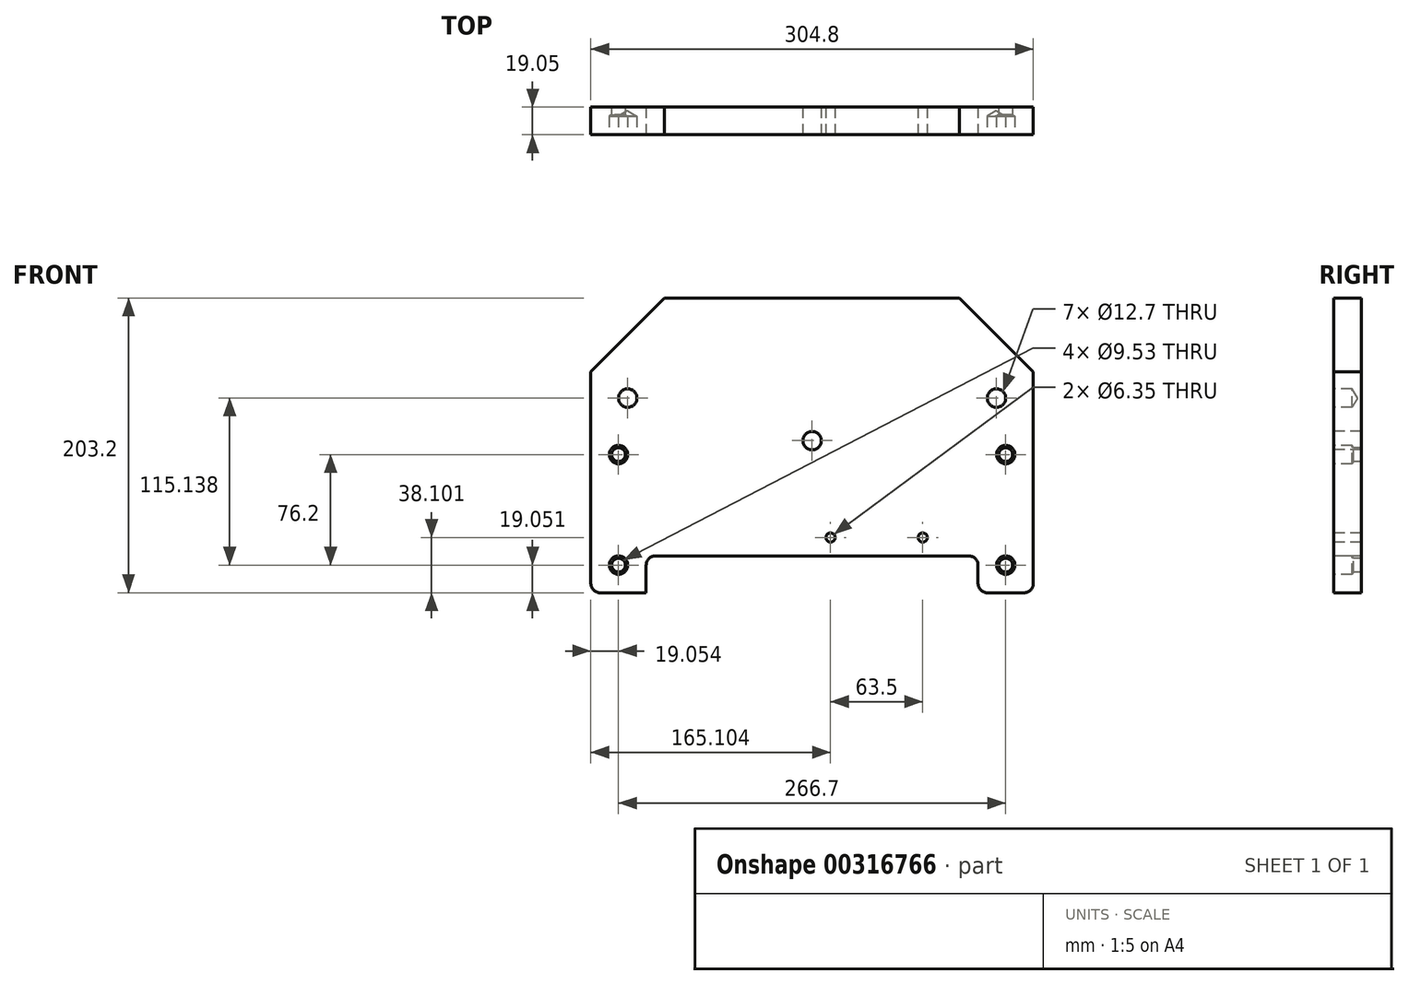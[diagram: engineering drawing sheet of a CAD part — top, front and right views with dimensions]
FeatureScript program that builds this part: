
annotation { "Feature Type Name" : "Feature", "Feature Type Description" : "" }
export const myFeature = defineFeature(function(context is Context, id is Id, definition is map)
    precondition{}
    {
        {
            var Q0;
            Q0=qCreatedBy(makeId("Front.planeOp"),FACE);
            var sketch = newSketch(context, id + "F0", { "sketchPlane" : qUnion([Q0])});
            skLineSegment(sketch, "E0.bottom", {"start": v(-130.02, 132.17) * mm, "end": v(174.78, 132.17) * mm});
            skLineSegment(sketch, "E0.top", {"start": v(-130.02, -71.03) * mm, "end": v(174.78, -71.03) * mm});
            skLineSegment(sketch, "E0.left", {"start": v(-130.02, 132.17) * mm, "end": v(-130.02, -71.03) * mm});
            skLineSegment(sketch, "E0.right", {"start": v(174.78, 132.17) * mm, "end": v(174.78, -71.03) * mm});
            skSolve(sketch);
        }
        {
            var Q0;
            Q0=makeQuery(id+"F0.imprint","IMPRINT",FACE,{"disambiguationData":[TD([[makeQuery(id+"F0.imprint","IMPRINT",EDGE,{"derivedFrom":sQuery(id+"F0.wireOp",EDGE,"E0.bottom")}),-1.0]])]});
            extrude(context, id + "F1", {"entities" : qUnion([Q0]), "depth" : 19.05 * mm});
        }
        {
            var Q0;
            Q0=makeQuery(id+"F1.opExtrude","SWEPT_EDGE",EDGE,{"disambiguationData":[OSD([sQuery(id+"F0.wireOp",EDGE,"E0.bottom"),sQuery(id+"F0.wireOp",EDGE,"E0.left")])]});
            var Q1;
            Q1=makeQuery(id+"F1.opExtrude","SWEPT_EDGE",EDGE,{"disambiguationData":[OSD([sQuery(id+"F0.wireOp",EDGE,"E0.bottom"),sQuery(id+"F0.wireOp",EDGE,"E0.right")])]});
            chamfer(context, id + "F2", {"entities" : qUnion([Q0, Q1]), "width" : 50.8 * mm, "tangentPropagation" : true});
        }
        {
            var Q0;
            Q0=makeQuery(id+"F1.opExtrude","CAP_FACE",FACE,{"disambiguationData":[OSD([sQuery(id+"F0.wireOp",EDGE,"E0.bottom"),sQuery(id+"F0.wireOp",EDGE,"E0.top"),sQuery(id+"F0.wireOp",EDGE,"E0.left"),sQuery(id+"F0.wireOp",EDGE,"E0.right")])],"isStart":false});
            var sketch = newSketch(context, id + "F3", { "sketchPlane" : qUnion([Q0])});
            skLineSegment(sketch, "E1.bottom", {"start": v(-91.92, -71.03) * mm, "end": v(136.68, -71.03) * mm});
            skLineSegment(sketch, "E1.top", {"start": v(-91.92, -45.63) * mm, "end": v(136.68, -45.63) * mm});
            skLineSegment(sketch, "E1.left", {"start": v(-91.92, -71.03) * mm, "end": v(-91.92, -45.63) * mm});
            skLineSegment(sketch, "E1.right", {"start": v(136.68, -71.03) * mm, "end": v(136.68, -45.63) * mm});
            skSolve(sketch);
        }
        {
            var Q0;
            Q0=makeQuery(id+"F3.imprint","IMPRINT",FACE,{"disambiguationData":[TD([[makeQuery(id+"F3.imprint","IMPRINT",EDGE,{"derivedFrom":sQuery(id+"F3.wireOp",EDGE,"E1.bottom")}),1.0]])]});
            extrude(context, id + "F4", {"entities" : qUnion([Q0]), "operationType" : NewBodyOperationType.REMOVE, "oppositeDirection" : true, "depth" : 19.05 * mm});
        }
        {
            var Q0;
            Q0=makeQuery(id+"F1.opExtrude","SWEPT_EDGE",EDGE,{"disambiguationData":[OSD([sQuery(id+"F0.wireOp",EDGE,"E0.top"),sQuery(id+"F0.wireOp",EDGE,"E0.left")])]});
            var Q1;
            Q1=makeQuery(id+"F4.boolean.opBoolean","COPY",EDGE,{"derivedFrom":makeQuery(id+"F4.opExtrude","SWEPT_EDGE",EDGE,{"disambiguationData":[OSD([sQuery(id+"F0.wireOp",EDGE,"E0.top"),sQuery(id+"F3.wireOp",EDGE,"E1.bottom"),sQuery(id+"F3.wireOp",EDGE,"E1.left")])]})});
            var Q2;
            Q2=makeQuery(id+"F4.boolean.opBoolean","COPY",EDGE,{"derivedFrom":makeQuery(id+"F4.opExtrude","SWEPT_EDGE",EDGE,{"disambiguationData":[OSD([sQuery(id+"F3.wireOp",EDGE,"E1.top"),sQuery(id+"F3.wireOp",EDGE,"E1.left")])]})});
            var Q3;
            Q3=makeQuery(id+"F4.boolean.opBoolean","COPY",EDGE,{"derivedFrom":makeQuery(id+"F4.opExtrude","SWEPT_EDGE",EDGE,{"disambiguationData":[OSD([sQuery(id+"F0.wireOp",EDGE,"E0.top"),sQuery(id+"F3.wireOp",EDGE,"E1.bottom"),sQuery(id+"F3.wireOp",EDGE,"E1.right")])]})});
            var Q4;
            Q4=makeQuery(id+"F1.opExtrude","SWEPT_EDGE",EDGE,{"disambiguationData":[OSD([sQuery(id+"F0.wireOp",EDGE,"E0.top"),sQuery(id+"F0.wireOp",EDGE,"E0.right")])]});
            var Q5;
            Q5=makeQuery(id+"F4.boolean.opBoolean","COPY",EDGE,{"derivedFrom":makeQuery(id+"F4.opExtrude","SWEPT_EDGE",EDGE,{"disambiguationData":[OSD([sQuery(id+"F3.wireOp",EDGE,"E1.top"),sQuery(id+"F3.wireOp",EDGE,"E1.right")])]})});
            fillet(context, id + "F5", {"entities" : qUnion([Q0, Q1, Q2, Q3, Q4, Q5]), "radius" : 6.35 * mm, "tangentPropagation" : true, "allowEdgeOverflow" : false});
        }
        {
            var Q0;
            Q0=makeQuery(id+"F1.opExtrude","CAP_FACE",FACE,{"disambiguationData":[OSD([sQuery(id+"F0.wireOp",EDGE,"E0.bottom"),sQuery(id+"F0.wireOp",EDGE,"E0.top"),sQuery(id+"F0.wireOp",EDGE,"E0.left"),sQuery(id+"F0.wireOp",EDGE,"E0.right")])],"isStart":false});
            var sketch = newSketch(context, id + "F6", { "sketchPlane" : qUnion([Q0])});
            skPoint(sketch, "E2", {"position": v(-110.97, -51.98) * mm});
            skPoint(sketch, "E3", {"position": v(155.73, -51.98) * mm});
            skPoint(sketch, "E4", {"position": v(-110.97, 24.22) * mm});
            skPoint(sketch, "E5", {"position": v(155.73, 24.22) * mm});
            skPoint(sketch, "E6", {"position": v(-104.62, 63.16) * mm});
            skPoint(sketch, "E7", {"position": v(149.38, 63.16) * mm});
            skPoint(sketch, "E8", {"position": v(35.08, -32.93) * mm});
            skPoint(sketch, "E9", {"position": v(98.58, -32.93) * mm});
            skPoint(sketch, "E10", {"position": v(22.38, 33.82) * mm});
            skSolve(sketch);
        }
        {
            var Q0;
            Q0=sQuery(id+"F6.wireOp",VERTEX,"E9");
            var Q1;
            Q1=sQuery(id+"F6.wireOp",VERTEX,"E8");
            var Q2;
            Q2=makeQuery(id+"F1.opExtrude","SWEPT_BODY",BODY,{"disambiguationData":[OSD([sQuery(id+"F0.wireOp",EDGE,"E0.bottom"),sQuery(id+"F0.wireOp",EDGE,"E0.top"),sQuery(id+"F0.wireOp",EDGE,"E0.left"),sQuery(id+"F0.wireOp",EDGE,"E0.right")])]});
            hole(context, id + "F7", {"style" : HoleStyle.SIMPLE, "endStyle" : HoleEndStyle.THROUGH, "holeDiameter" : 6.35 * mm, "tappedDepth" : 12.7 * mm, "tapClearance" : 3, "locations" : qUnion([Q0, Q1]), "scope" : qUnion([Q2])});
        }
        {
            var Q0;
            Q0=sQuery(id+"F6.wireOp",VERTEX,"E6");
            var Q1;
            Q1=sQuery(id+"F6.wireOp",VERTEX,"E7");
            var Q2;
            Q2=sQuery(id+"F6.wireOp",VERTEX,"E4");
            var Q3;
            Q3=sQuery(id+"F6.wireOp",VERTEX,"E5");
            var Q4;
            Q4=sQuery(id+"F6.wireOp",VERTEX,"E3");
            var Q5;
            Q5=sQuery(id+"F6.wireOp",VERTEX,"E2");
            var Q6;
            Q6=makeQuery(id+"F1.opExtrude","SWEPT_BODY",BODY,{"disambiguationData":[OSD([sQuery(id+"F0.wireOp",EDGE,"E0.bottom"),sQuery(id+"F0.wireOp",EDGE,"E0.top"),sQuery(id+"F0.wireOp",EDGE,"E0.left"),sQuery(id+"F0.wireOp",EDGE,"E0.right")])]});
            hole(context, id + "F8", {"style" : HoleStyle.SIMPLE, "endStyle" : HoleEndStyle.BLIND, "holeDiameter" : 12.7 * mm, "holeDepth" : 12.7 * mm, "tappedDepth" : 12.7 * mm, "tapClearance" : 3, "locations" : qUnion([Q0, Q1, Q2, Q3, Q4, Q5]), "scope" : qUnion([Q6])});
        }
        {
            var Q0;
            Q0=sQuery(id+"F6.wireOp",VERTEX,"E4");
            var Q1;
            Q1=sQuery(id+"F6.wireOp",VERTEX,"E5");
            var Q2;
            Q2=sQuery(id+"F6.wireOp",VERTEX,"E3");
            var Q3;
            Q3=sQuery(id+"F6.wireOp",VERTEX,"E2");
            var Q4;
            Q4=makeQuery(id+"F1.opExtrude","SWEPT_BODY",BODY,{"disambiguationData":[OSD([sQuery(id+"F0.wireOp",EDGE,"E0.bottom"),sQuery(id+"F0.wireOp",EDGE,"E0.top"),sQuery(id+"F0.wireOp",EDGE,"E0.left"),sQuery(id+"F0.wireOp",EDGE,"E0.right")])]});
            hole(context, id + "F9", {"style" : HoleStyle.SIMPLE, "endStyle" : HoleEndStyle.THROUGH, "holeDiameter" : 9.52 * mm, "tappedDepth" : 12.7 * mm, "tapClearance" : 3, "locations" : qUnion([Q0, Q1, Q2, Q3]), "scope" : qUnion([Q4])});
        }
        {
            var Q0;
            Q0=sQuery(id+"F6.wireOp",VERTEX,"E10");
            var Q1;
            Q1=makeQuery(id+"F1.opExtrude","SWEPT_BODY",BODY,{"disambiguationData":[OSD([sQuery(id+"F0.wireOp",EDGE,"E0.bottom"),sQuery(id+"F0.wireOp",EDGE,"E0.top"),sQuery(id+"F0.wireOp",EDGE,"E0.left"),sQuery(id+"F0.wireOp",EDGE,"E0.right")])]});
            hole(context, id + "F10", {"style" : HoleStyle.SIMPLE, "endStyle" : HoleEndStyle.THROUGH, "holeDiameter" : 12.7 * mm, "tappedDepth" : 12.7 * mm, "tapClearance" : 3, "locations" : qUnion([Q0]), "scope" : qUnion([Q1])});
        }
    });
